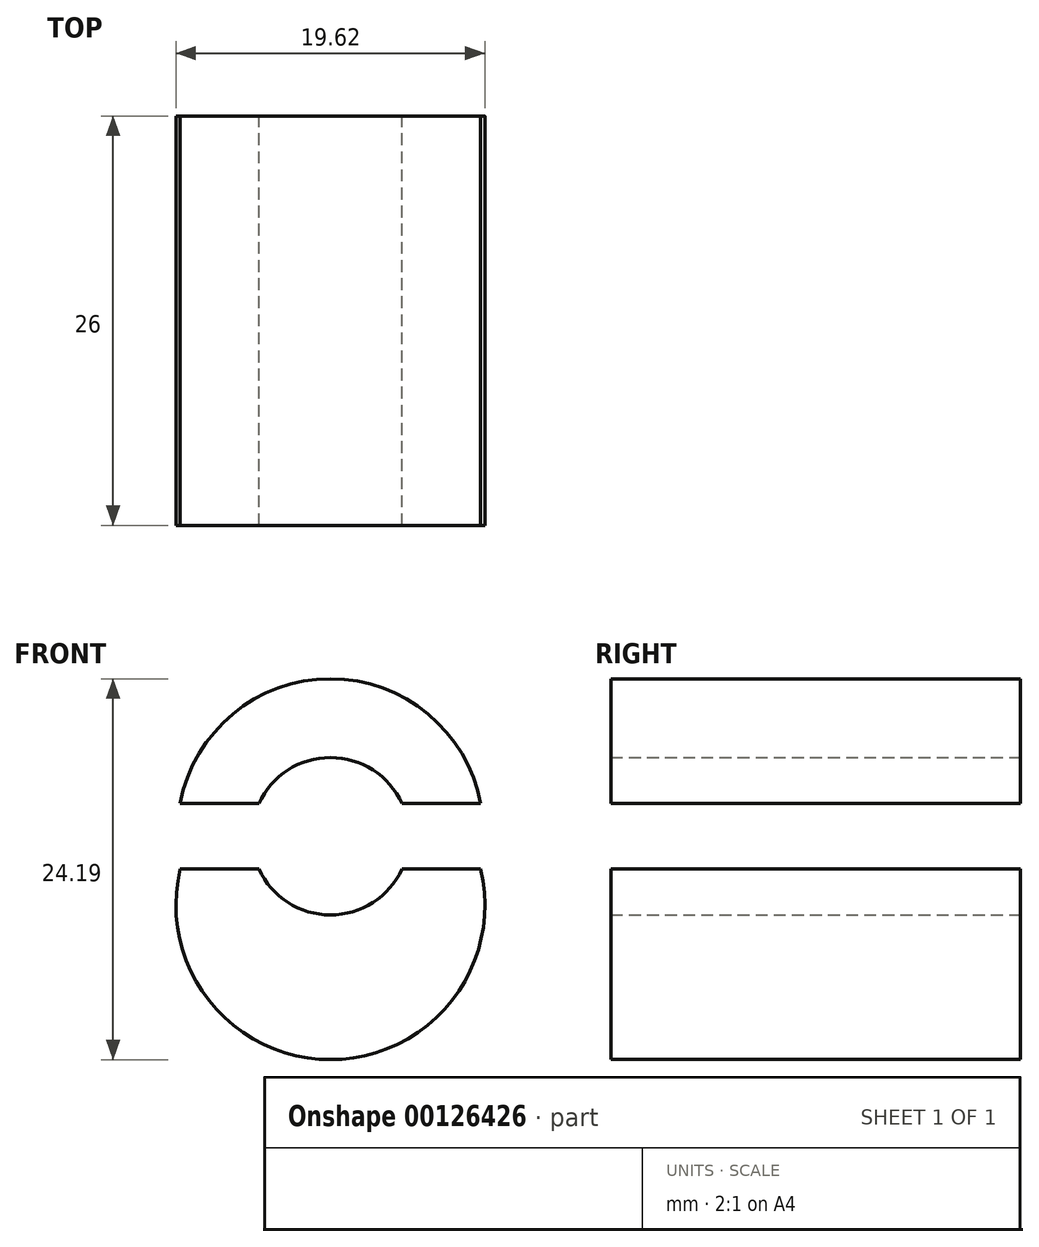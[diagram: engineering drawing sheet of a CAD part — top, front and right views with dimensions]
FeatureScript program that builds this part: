
annotation { "Feature Type Name" : "Feature", "Feature Type Description" : "" }
export const myFeature = defineFeature(function(context is Context, id is Id, definition is map)
    precondition{}
    {
        {
            var Q0;
            Q0=qCreatedBy(makeId("Front.planeOp"),FACE);
            var sketch = newSketch(context, id + "F0", { "sketchPlane" : qUnion([Q0])});
            skCircle(sketch, "E0", {"center": v(0, 0) * mm, "radius": 5 * mm});
            skLineSegment(sketch, "E1", {"start": v(0, 5) * mm, "end": v(0, 10) * mm});
            skLineSegment(sketch, "E2", {"start": v(-4.54, 2.09) * mm, "end": v(-9.54, 2.09) * mm});
            skLineSegment(sketch, "E3", {"start": v(4.54, 2.09) * mm, "end": v(9.54, 2.09) * mm});
            skLineSegment(sketch, "E4", {"start": v(-4.54, -2.09) * mm, "end": v(-9.54, -2.09) * mm});
            skLineSegment(sketch, "E5", {"start": v(4.54, -2.09) * mm, "end": v(9.54, -2.09) * mm});
            skArc(sketch, "E6", {"start": v(9.54, 2.09) * mm, "mid": v(0, 10) * mm, "end": v(-9.54, 2.09) * mm});
            skLineSegment(sketch, "E7", {"start": v(0, -5) * mm, "end": v(0, -10) * mm});
            skArc(sketch, "E8", {"start": v(-9.54, -2.09) * mm, "mid": v(0, -14.19) * mm, "end": v(9.54, -2.09) * mm});
            skSolve(sketch);
        }
        {
            var Q0;
            {var subQ0=sQuery(id+"F0.wireOp",EDGE,"E1");Q0=makeQuery(id+"F0.imprint","IMPRINT",FACE,{"disambiguationData":[TD([[makeQuery(id+"F0.imprint","IMPRINT",EDGE,{"derivedFrom":subQ0}),-1.0]])]});}
            var Q1;
            {var subQ0=sQuery(id+"F0.wireOp",EDGE,"E1");Q1=makeQuery(id+"F0.imprint","IMPRINT",FACE,{"disambiguationData":[TD([[makeQuery(id+"F0.imprint","IMPRINT",EDGE,{"derivedFrom":subQ0}),1.0]])]});}
            var Q2;
            {var subQ0=sQuery(id+"F0.wireOp",EDGE,"E4");Q2=makeQuery(id+"F0.imprint","IMPRINT",FACE,{"disambiguationData":[TD([[makeQuery(id+"F0.imprint","IMPRINT",EDGE,{"derivedFrom":subQ0}),1.0]])]});}
            var Q3;
            {var subQ0=sQuery(id+"F0.wireOp",EDGE,"E5");Q3=makeQuery(id+"F0.imprint","IMPRINT",FACE,{"disambiguationData":[TD([[makeQuery(id+"F0.imprint","IMPRINT",EDGE,{"derivedFrom":subQ0}),-1.0]])]});}
            extrude(context, id + "F1", {"entities" : qUnion([Q0, Q1, Q2, Q3]), "depth" : 26 * mm});
        }
    });
